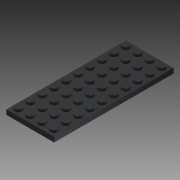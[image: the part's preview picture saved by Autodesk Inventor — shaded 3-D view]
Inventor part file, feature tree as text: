
AUTODESK INVENTOR PART (.ipt)
format: ipt  version: 2013 (Build 170138000, 138)  size: 240,640 bytes
history: native  units: mm
features: extrude x3, sketch x1, pattern_linear x1
ambient origin geometry x8: Origin, YZ Plane, XZ Plane, XY Plane, X Axis, Y Axis, Z Axis, Center Point
bodies: Solid1 (feature_tree)
feature tree (5):
  sketch  "Sketch1"  dims[d0=8.0mm d1=8.0mm d2=4.8mm d3=3.2mm d4=0.0mm d5=4.9mm d6=0.0mm d7=1.7mm d8=0.0mm d9=100.0mm d11=8.0mm d22=40.0mm d24=8.0mm]
  extrude  "Extrusion1"  Depth=8.0mm
  extrude  "Extrusion2"  Depth=4.8mm
  extrude  "Extrusion3"  Depth=3.2mm TaperAngle=0.0deg
  pattern_linear  "Rectangular Pattern1"  Spacing1=4.9mm  [1 undecoded]
note: 1 required parameter value undecoded (feature->parameter linkage not recoverable at this tier; creation-order binding heuristic only, values carry confidence <= 0.55)
